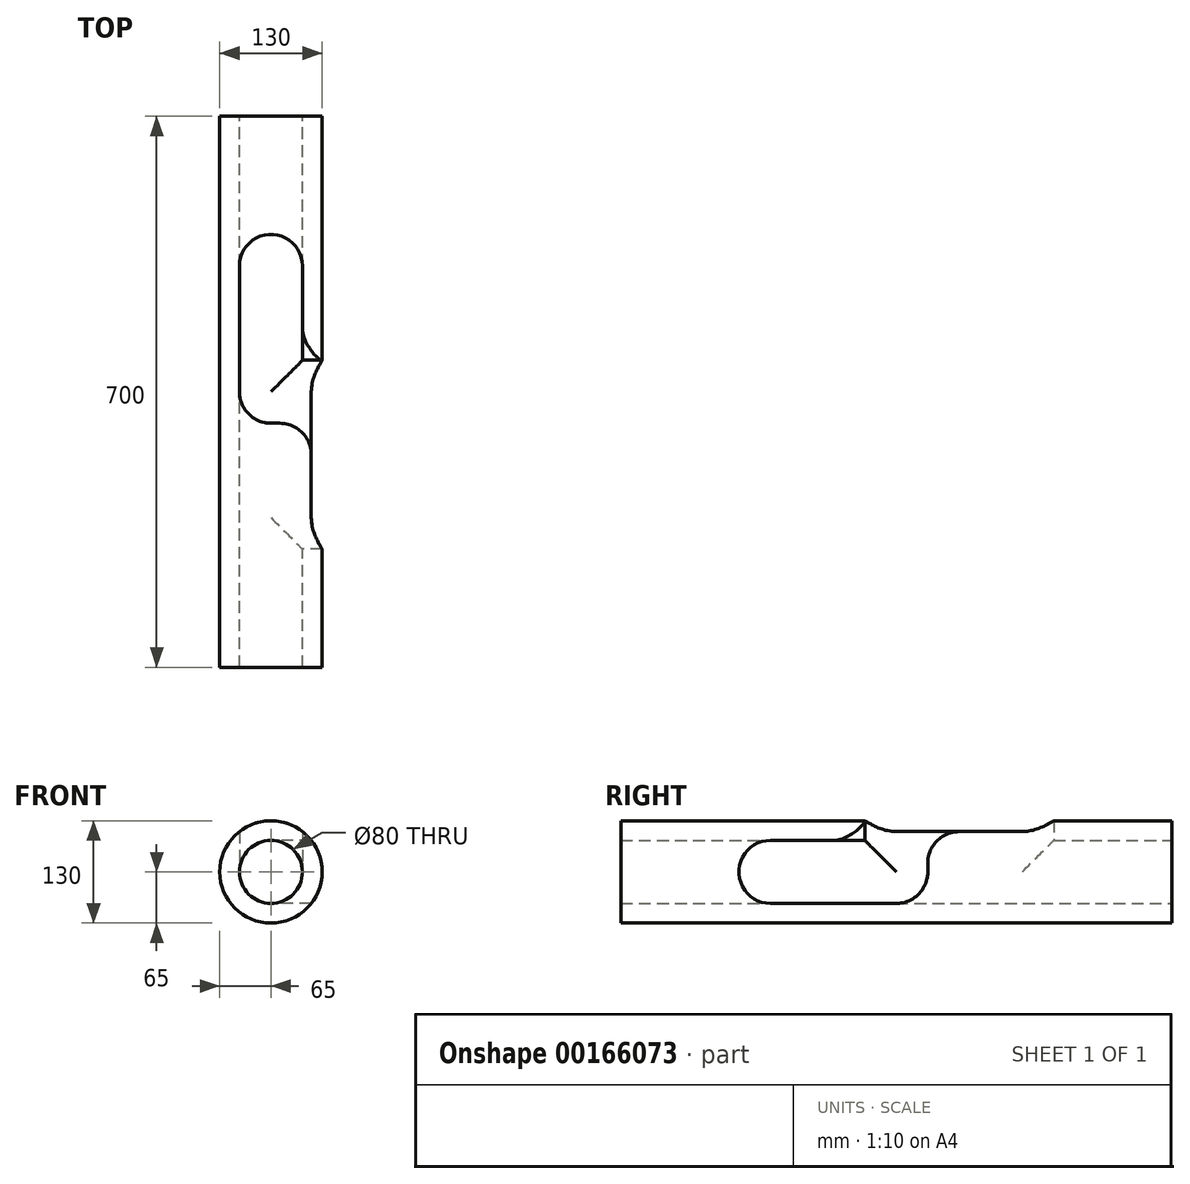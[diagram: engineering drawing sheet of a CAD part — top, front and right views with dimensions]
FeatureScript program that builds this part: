
annotation { "Feature Type Name" : "Feature", "Feature Type Description" : "" }
export const myFeature = defineFeature(function(context is Context, id is Id, definition is map)
    precondition{}
    {
        {
            var Q0;
            Q0=qCreatedBy(makeId("Front.planeOp"),FACE);
            var sketch = newSketch(context, id + "F0", { "sketchPlane" : qUnion([Q0])});
            skCircle(sketch, "E0", {"center": v(0, 0) * mm, "radius": 65 * mm});
            skCircle(sketch, "E1", {"center": v(0, 0) * mm, "radius": 40 * mm});
            skSolve(sketch);
        }
        {
            var Q0;
            Q0 = qSketchRegion(id + "F0", true);
            extrude(context, id + "F1", {"entities" : qUnion([Q0]), "endBound" : BoundingType.SYMMETRIC, "depth" : 700 * mm});
        }
        {
            var Q0;
            Q0=qCreatedBy(makeId("Top.planeOp"),FACE);
            var sketch = newSketch(context, id + "F2", { "sketchPlane" : qUnion([Q0])});
            skCircle(sketch, "E2", {"center": v(0, 160) * mm, "radius": 40 * mm});
            skLineSegment(sketch, "E3", {"start": v(-40, 160) * mm, "end": v(-40, -40) * mm});
            skLineSegment(sketch, "E4.0", {"start": v(65, 350) * mm, "end": v(-65, 350) * mm, "construction": true});
            skLineSegment(sketch, "E5.1", {"start": v(65, -350) * mm, "end": v(-65, -350) * mm, "construction": true});
            skLineSegment(sketch, "E6", {"start": v(65, 350) * mm, "end": v(65, -350) * mm, "construction": true});
            skLineSegment(sketch, "E7", {"start": v(40, 160) * mm, "end": v(40, 40) * mm});
            skLineSegment(sketch, "E8", {"start": v(40, 40) * mm, "end": v(65, 40) * mm});
            skLineSegment(sketch, "E9", {"start": v(65, 40) * mm, "end": v(65, -40) * mm});
            skLineSegment(sketch, "E10", {"start": v(-40, -40) * mm, "end": v(65, -40) * mm});
            skLineSegment(sketch, "E11", {"start": v(-104.85, 0) * mm, "end": v(282.03, 0) * mm, "construction": true});
            skSolve(sketch);
        }
        {
            var Q0;
            Q0 = qSketchRegion(id + "F2", true);
            extrude(context, id + "F3", {"entities" : qUnion([Q0]), "operationType" : NewBodyOperationType.REMOVE, "endBound" : BoundingType.THROUGH_ALL, "depth" : 25 * mm});
        }
        {
            var Q0;
            Q0=qCreatedBy(makeId("Right.planeOp"),FACE);
            var sketch = newSketch(context, id + "F4", { "sketchPlane" : qUnion([Q0])});
            skLineSegment(sketch, "E12.0", {"start": v(350, -65) * mm, "end": v(350, 65) * mm, "construction": true});
            skLineSegment(sketch, "E13.0", {"start": v(-350, -65) * mm, "end": v(-350, 65) * mm, "construction": true});
            skLineSegment(sketch, "E14", {"start": v(350, 65) * mm, "end": v(-350, 65) * mm, "construction": true});
            skCircle(sketch, "E15", {"center": v(-160, 0) * mm, "radius": 40 * mm});
            skLineSegment(sketch, "E16.0", {"start": v(-40, 65) * mm, "end": v(-40, 0) * mm, "construction": true});
            skLineSegment(sketch, "E17.0", {"start": v(40, 51.23) * mm, "end": v(40, 0) * mm, "construction": true});
            skLineSegment(sketch, "E18", {"start": v(-160, 40) * mm, "end": v(-40, 40) * mm});
            skLineSegment(sketch, "E19", {"start": v(-40, 40) * mm, "end": v(-40, 65) * mm});
            skLineSegment(sketch, "E20", {"start": v(40, 65) * mm, "end": v(40, -40) * mm});
            skLineSegment(sketch, "E21", {"start": v(40, -40) * mm, "end": v(-160, -40) * mm});
            skLineSegment(sketch, "E22", {"start": v(40, 65) * mm, "end": v(-40, 65) * mm});
            skSolve(sketch);
        }
        {
            var Q0;
            Q0 = qSketchRegion(id + "F4", true);
            extrude(context, id + "F5", {"entities" : qUnion([Q0]), "operationType" : NewBodyOperationType.REMOVE, "endBound" : BoundingType.THROUGH_ALL, "depth" : 25 * mm});
        }
        {
            var Q0;
            Q0=makeQuery(id+"F5.boolean.opBoolean","COPY",EDGE,{"derivedFrom":makeQuery(id+"F5.opExtrude","SWEPT_EDGE",EDGE,{"disambiguationData":[OSD([sQuery(id+"F4.wireOp",EDGE,"E20"),sQuery(id+"F4.wireOp",EDGE,"E21")])]})});
            var Q1;
            Q1=makeQuery(id+"F3.boolean.opBoolean","COPY",EDGE,{"derivedFrom":makeQuery(id+"F3.opExtrude","SWEPT_EDGE",EDGE,{"disambiguationData":[OSD([sQuery(id+"F2.wireOp",EDGE,"E3"),sQuery(id+"F2.wireOp",EDGE,"E10")])]})});
            fillet(context, id + "F6", {"entities" : qUnion([Q0, Q1]), "radius" : 40 * mm, "tangentPropagation" : true, "allowEdgeOverflow" : false});
        }
        {
            var Q0;
            Q0=qCreatedBy(makeId("Top.planeOp"),FACE);
            var sketch = newSketch(context, id + "F7", { "sketchPlane" : qUnion([Q0])});
            skLineSegment(sketch, "E23.0", {"start": v(51.23, -160) * mm, "end": v(51.23, -40) * mm, "construction": true});
            skLineSegment(sketch, "E24.0", {"start": v(0, -40) * mm, "end": v(51.23, -40) * mm, "construction": true});
            skArc(sketch, "E25", {"start": v(51.23, -80) * mm, "mid": v(39.52, -51.72) * mm, "end": v(11.23, -40) * mm});
            skLineSegment(sketch, "E26", {"start": v(11.23, -40) * mm, "end": v(51.23, -40) * mm});
            skLineSegment(sketch, "E27", {"start": v(51.23, -40) * mm, "end": v(51.23, -80) * mm});
            skSolve(sketch);
        }
        {
            var Q0;
            Q0 = qSketchRegion(id + "F7", true);
            extrude(context, id + "F8", {"entities" : qUnion([Q0]), "operationType" : NewBodyOperationType.REMOVE, "endBound" : BoundingType.THROUGH_ALL, "depth" : 25 * mm});
        }
        {
            var Q0;
            Q0=qCreatedBy(makeId("Right.planeOp"),FACE);
            var sketch = newSketch(context, id + "F9", { "sketchPlane" : qUnion([Q0])});
            skLineSegment(sketch, "E28.0", {"start": v(40, 51.23) * mm, "end": v(40, 0) * mm, "construction": true});
            skLineSegment(sketch, "E29.0", {"start": v(160, 51.23) * mm, "end": v(40, 51.23) * mm, "construction": true});
            skArc(sketch, "E30", {"start": v(80, 51.23) * mm, "mid": v(51.72, 39.52) * mm, "end": v(40, 11.23) * mm});
            skLineSegment(sketch, "E31", {"start": v(80, 51.23) * mm, "end": v(40, 51.23) * mm});
            skLineSegment(sketch, "E32", {"start": v(40, 0) * mm, "end": v(40, 51.23) * mm});
            skSolve(sketch);
        }
        {
            var Q0;
            Q0 = qSketchRegion(id + "F9", true);
            extrude(context, id + "F10", {"entities" : qUnion([Q0]), "operationType" : NewBodyOperationType.REMOVE, "endBound" : BoundingType.THROUGH_ALL, "depth" : 25 * mm});
        }
    });
